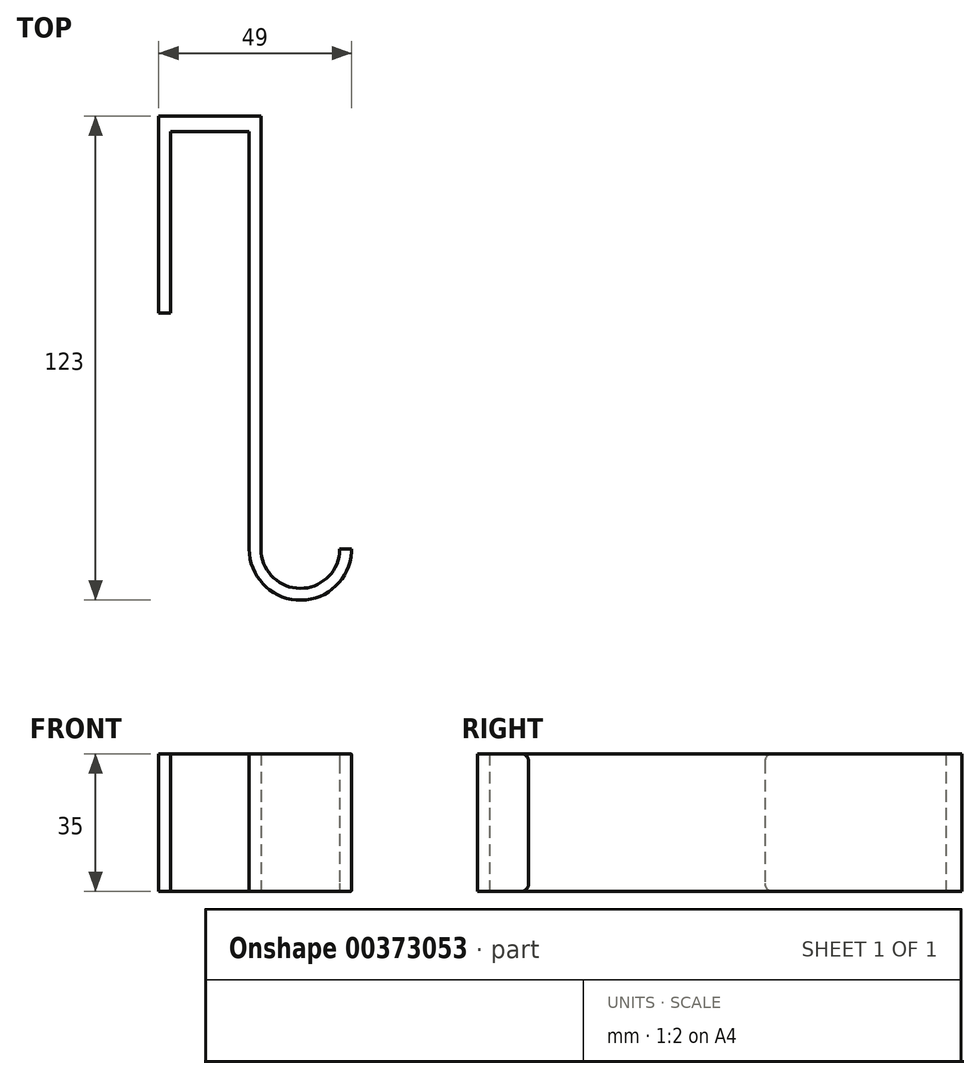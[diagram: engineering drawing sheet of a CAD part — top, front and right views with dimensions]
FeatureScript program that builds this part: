
annotation { "Feature Type Name" : "Feature", "Feature Type Description" : "" }
export const myFeature = defineFeature(function(context is Context, id is Id, definition is map)
    precondition{}
    {
        {
            var Q0;
            Q0=qCreatedBy(makeId("Top.planeOp"),FACE);
            var sketch = newSketch(context, id + "F0", { "sketchPlane" : qUnion([Q0])});
            skLineSegment(sketch, "E0", {"start": v(0, 0) * mm, "end": v(0, 50) * mm});
            skLineSegment(sketch, "E1", {"start": v(26, 50) * mm, "end": v(26, -60) * mm});
            skLineSegment(sketch, "E2", {"start": v(26, 50) * mm, "end": v(0, 50) * mm});
            skArc(sketch, "E3", {"start": v(26, -60) * mm, "mid": v(36, -70) * mm, "end": v(46, -60) * mm});
            skLineSegment(sketch, "E4.0", {"start": v(3, 0) * mm, "end": v(3, 46) * mm});
            skLineSegment(sketch, "E4.1", {"start": v(23, 46) * mm, "end": v(3, 46) * mm});
            skLineSegment(sketch, "E4.2", {"start": v(23, 46) * mm, "end": v(23, -60) * mm});
            skArc(sketch, "E4.3", {"start": v(23, -60) * mm, "mid": v(36, -73) * mm, "end": v(49, -60) * mm});
            skLineSegment(sketch, "E5", {"start": v(3, 0) * mm, "end": v(0, 0) * mm});
            skLineSegment(sketch, "E6", {"start": v(49, -60) * mm, "end": v(46, -60) * mm});
            skSolve(sketch);
        }
        {
            var Q0;
            Q0=makeQuery(id+"F0.imprint","IMPRINT",FACE,{"disambiguationData":[TD([[makeQuery(id+"F0.imprint","IMPRINT",EDGE,{"derivedFrom":sQuery(id+"F0.wireOp",EDGE,"E0")}),-1.0]])]});
            extrude(context, id + "F1", {"entities" : qUnion([Q0]), "depth" : 35 * mm});
        }
        {
            var Q0;
            Q0=makeQuery(id+"F1.opExtrude","CAP_EDGE",EDGE,{"disambiguationData":[OSD([sQuery(id+"F0.wireOp",EDGE,"E6")])],"isStart":false});
            var Q1;
            Q1=makeQuery(id+"F1.opExtrude","CAP_EDGE",EDGE,{"disambiguationData":[OSD([sQuery(id+"F0.wireOp",EDGE,"E6")])],"isStart":true});
            var Q2;
            Q2=makeQuery(id+"F1.opExtrude","CAP_EDGE",EDGE,{"disambiguationData":[OSD([sQuery(id+"F0.wireOp",EDGE,"E5")])],"isStart":false});
            var Q3;
            Q3=makeQuery(id+"F1.opExtrude","CAP_EDGE",EDGE,{"disambiguationData":[OSD([sQuery(id+"F0.wireOp",EDGE,"E5")])],"isStart":true});
            fillet(context, id + "F2", {"entities" : qUnion([Q0, Q1, Q2, Q3]), "radius" : 2 * mm, "tangentPropagation" : true, "allowEdgeOverflow" : false});
        }
    });
